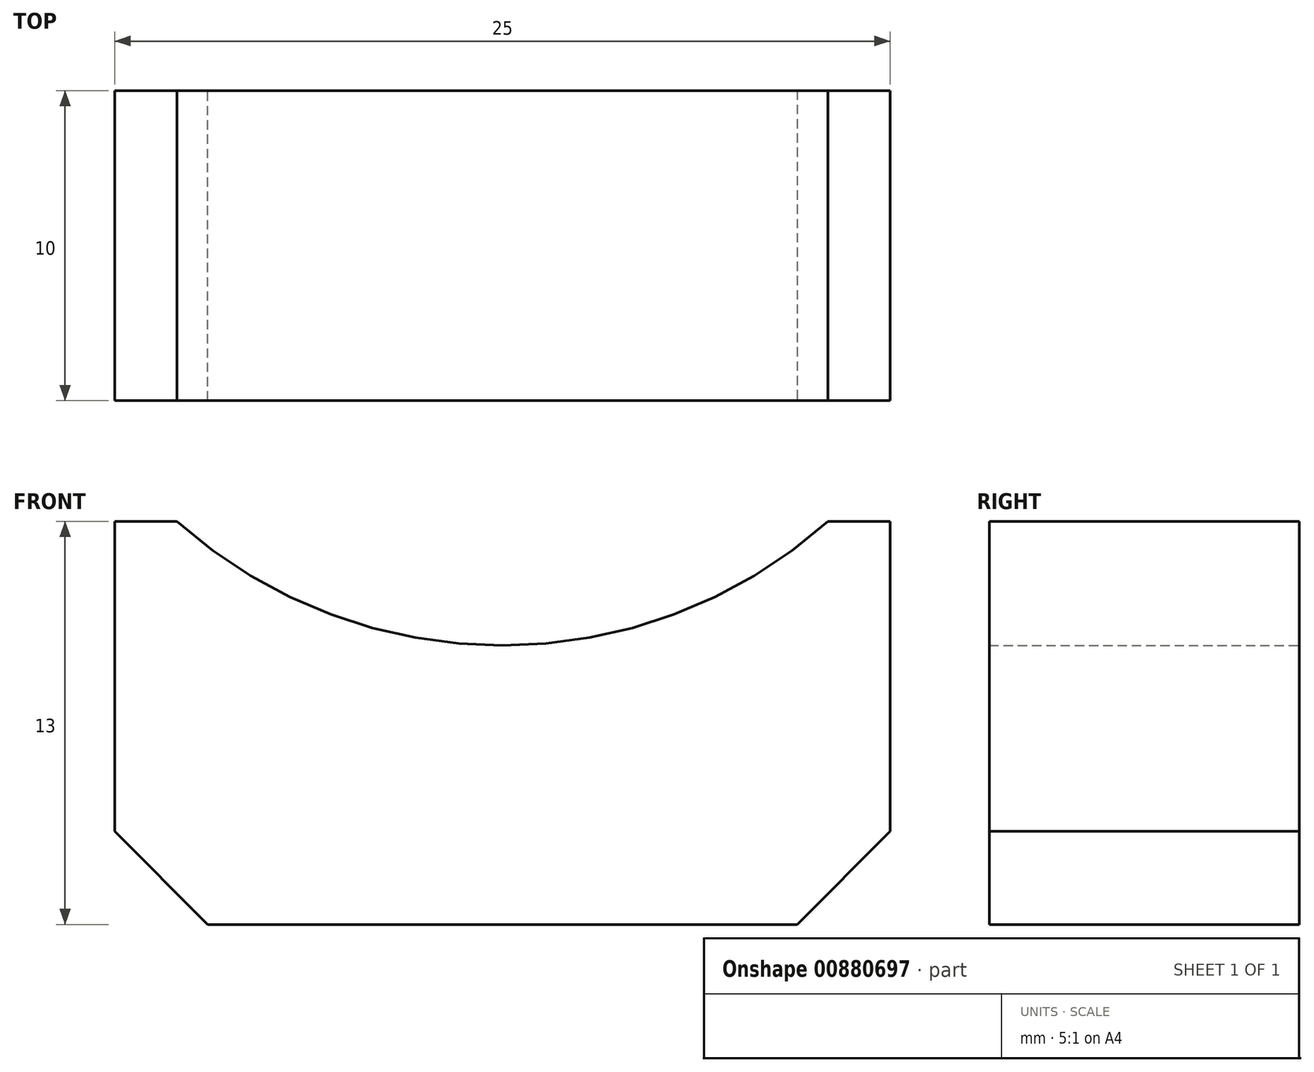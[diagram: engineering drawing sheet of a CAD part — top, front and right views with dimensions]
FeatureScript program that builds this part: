
annotation { "Feature Type Name" : "Feature", "Feature Type Description" : "" }
export const myFeature = defineFeature(function(context is Context, id is Id, definition is map)
    precondition{}
    {
        {
            var Q0;
            Q0=qCreatedBy(makeId("Front.planeOp"),FACE);
            var sketch = newSketch(context, id + "F0", { "sketchPlane" : qUnion([Q0])});
            skLineSegment(sketch, "E0.bottom", {"start": v(0, 13) * mm, "end": v(2, 13) * mm});
            skLineSegment(sketch, "E0.top", {"start": v(0, 0) * mm, "end": v(25, 0) * mm});
            skLineSegment(sketch, "E0.left", {"start": v(0, 13) * mm, "end": v(0, 0) * mm});
            skLineSegment(sketch, "E0.right", {"start": v(25, 13) * mm, "end": v(25, 0) * mm});
            skLineSegment(sketch, "E1", {"start": v(12.5, 25.82) * mm, "end": v(12.5, 9) * mm, "construction": true});
            skPoint(sketch, "E1.startSnap0", {"position": v(12.5, 13) * mm});
            skLineSegment(sketch, "E2", {"start": v(12.5, 9) * mm, "end": v(12.5, -10.7) * mm, "construction": true});
            skArc(sketch, "E3", {"start": v(2, 13) * mm, "mid": v(12.5, 9) * mm, "end": v(23, 13) * mm});
            skLineSegment(sketch, "E4.trimOffspring", {"start": v(23, 13) * mm, "end": v(25, 13) * mm});
            skSolve(sketch);
        }
        {
            var Q0;
            Q0=makeQuery(id+"F0.imprint","IMPRINT",FACE,{"disambiguationData":[TD([[makeQuery(id+"F0.imprint","IMPRINT",EDGE,{"derivedFrom":sQuery(id+"F0.wireOp",EDGE,"E0.bottom")}),-1.0]])]});
            extrude(context, id + "F1", {"entities" : qUnion([Q0]), "depth" : 10 * mm, "offsetDistance" : 25 * mm});
        }
        {
            var Q0;
            Q0=makeQuery(id+"F1.opExtrude","SWEPT_EDGE",EDGE,{"disambiguationData":[OSD([sQuery(id+"F0.wireOp",EDGE,"E0.top"),sQuery(id+"F0.wireOp",EDGE,"E0.right")])]});
            chamfer(context, id + "F2", {"entities" : qUnion([Q0]), "width" : 3 * mm, "tangentPropagation" : true});
        }
        {
            var Q0;
            Q0=makeQuery(id+"F1.opExtrude","SWEPT_EDGE",EDGE,{"disambiguationData":[OSD([sQuery(id+"F0.wireOp",EDGE,"E0.top"),sQuery(id+"F0.wireOp",EDGE,"E0.left")])]});
            chamfer(context, id + "F3", {"entities" : qUnion([Q0]), "width" : 3 * mm, "tangentPropagation" : true});
        }
    });
